# Revit family: RN 36010 Valvola di regolazione di flusso
name_source: partatom
category: Rohrzubehör
units: mm (PartAtom-declared; Revit-internal decimal feet)

## family parameters
Arbeitsebenenbasiert = Nein
Beim Laden mit Abzugskörper schneiden = Nein
Bemaßung runder Anschluss = Durchmesser verwenden
Gemeinsam genutzt = Nein
Immer vertikal = Ja
Teiletyp = Ventil - Zerlegung in

## types (2) — shared parameters
1.010.00.2 Blattnummer der Richtlinie = 17
1.010.00.3 Ausgabedatum (Monat) der Richtlinie = 201601
1.010.00.4 Herstellername = R. Nussbaum AG
1.010.00.5 Revisionsdatum der Datei = 20190528
1.010.00.6 Webadresse des Herstellers = http://www.nussbaum.ch
1.100.00.3 Sortiernummer für Anzeigereihenfolge = 2
1.100.00.4 Produktbezeichnung = Regulierarmaturen (Drosselarmaturen)
1.960/3L.00.8 Link (URL) = https://www.nussbaum.ch
17.700.00.10 Tmax.Regelung [°C] = 65
17.700.00.11 Maximaler Differenzdruck Δpmax (über dem Ventil) [1.0 · 102 Pa] = 1000
17.700.00.4 Armaturentyp = 3
17.700.00.7 Maximale Betriebstemperatur TB [°C] = 90
17.700.00.8 Maximaler Betriebsdruck (Arbeitsdruck) ps [1.0 · 105 Pa] = 10
17.700.00.9 Tmin.Regelung [°C] = 40
Connector Visibility = Nein
EnclosingSpace Visibility = Nein
Hersteller = R. Nussbauzm AG
URL = https://www.nussbaum.ch

## per-type parameters (varying)
| type | 1.800.00.3 TGA-Nummer | 1.810.00.3 Hersteller-Bestellnummer | 1.810.00.4 DATANORM-Nummer | 1.810.00.5 StLB-Nummer | 1.810.00.6 GTIN-Nummer | 17.700.00.30 Produktbeschreibung | 17.700.00.5 Nennweite DN | 17.700.00.6 kvs-Wert [m3/h] | CONNECTOR0_DIAMETER_dX_0r | CONNECTOR0_dX_00 | CONNECTOR0_dX_01 | CONNECTOR0_ref_dX | CONNECTOR1_DIAMETER_dX_0r | CONNECTOR1_dX_00 | CONNECTOR1_dX_01 | CONNECTOR1_ref_dX | Modell | R. Nussbaum AG 36010.35 de Visibility | R. Nussbaum AG 36010.36 de Visibility | Typenkommentare |
| DN 15 | 00200200000000000000000000000200700000000000000001???????? | 36010.35 | 36010.35 | 643.171 | 7612945694409 | 36010.35, Geregeltes Zirkulationsventil, ohne Anschlussverschraubungen, DN=15 | 15 | 1.542 | 20 mm | 43 mm | 34 mm | 43 mm | 20 mm | 33 mm | 42 mm | 42 mm | 36010.35 | Ja | Nein | Valvola di regolazione di flussoDN 15 |
| DN 20 | 00200300000000000000000000000200700000000000000002000????? | 36010.36 | 36010.36 | 643.172 | 7612945694393 | 36010.36, Geregeltes Zirkulationsventil, ohne Anschlussverschraubungen, DN=20 | 20 | 1.56 | 25 mm  [stored 0.082021 ft] | 46 mm | 37 mm | 46 mm | 25 mm  [stored 0.082021 ft] | 38 mm | 47 mm | 47 mm | 36010.36 | Nein | Ja | Valvola di regolazione di flussoDN 20 |

note: [stored X ft] marks values corroborated as IEEE doubles in the binary element streams (Revit-internal decimal feet)

## geometry (parser evidence)
native form markers: Sweep x1
no freeform markers — native parametric forms only
